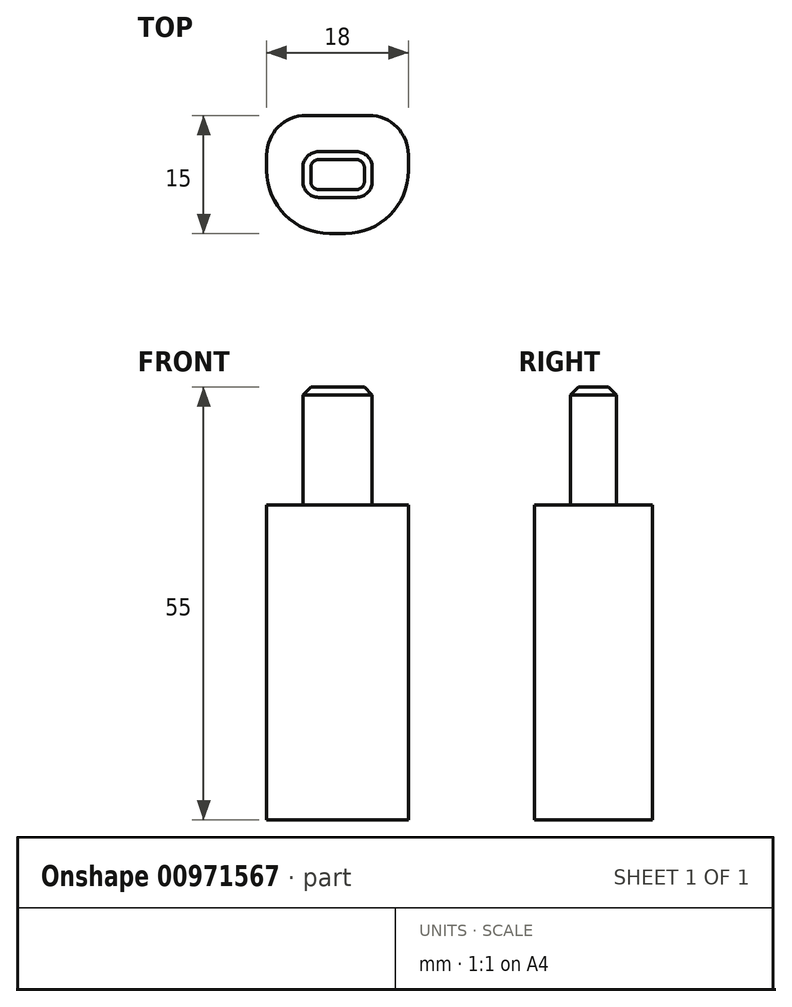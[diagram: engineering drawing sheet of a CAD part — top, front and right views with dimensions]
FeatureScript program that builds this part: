
annotation { "Feature Type Name" : "Feature", "Feature Type Description" : "" }
export const myFeature = defineFeature(function(context is Context, id is Id, definition is map)
    precondition{}
    {
        {
            var Q0;
            Q0=qCreatedBy(makeId("Top.planeOp"),FACE);
            var sketch = newSketch(context, id + "F0", { "sketchPlane" : qUnion([Q0])});
            skLineSegment(sketch, "E0.bottom", {"start": v(-4, 7.5) * mm, "end": v(4, 7.5) * mm});
            skLineSegment(sketch, "E0.top", {"start": v(-1, -7.5) * mm, "end": v(1, -7.5) * mm});
            skLineSegment(sketch, "E0.left", {"start": v(-9, 2.5) * mm, "end": v(-9, 0.5) * mm});
            skLineSegment(sketch, "E0.right", {"start": v(9, 2.5) * mm, "end": v(9, 0.5) * mm});
            skLineSegment(sketch, "E1", {"start": v(-9, -7.5) * mm, "end": v(9, 7.5) * mm, "construction": true});
            skPoint(sketch, "E2.visualSharp", {"position": v(-9, 7.5) * mm});
            skArc(sketch, "E2.filletArc", {"start": v(-4, 7.5) * mm, "mid": v(-7.54, 6.04) * mm, "end": v(-9, 2.5) * mm});
            skPoint(sketch, "E3.visualSharp", {"position": v(9, 7.5) * mm});
            skArc(sketch, "E3.filletArc", {"start": v(9, 2.5) * mm, "mid": v(7.54, 6.04) * mm, "end": v(4, 7.5) * mm});
            skPoint(sketch, "E4.visualSharp", {"position": v(9, -7.5) * mm});
            skArc(sketch, "E4.filletArc", {"start": v(1, -7.5) * mm, "mid": v(6.66, -5.16) * mm, "end": v(9, 0.5) * mm});
            skPoint(sketch, "E5.visualSharp", {"position": v(-9, -7.5) * mm});
            skArc(sketch, "E5.filletArc", {"start": v(-9, 0.5) * mm, "mid": v(-6.66, -5.16) * mm, "end": v(-1, -7.5) * mm});
            skLineSegment(sketch, "E6.bottom", {"start": v(-2.4, 2.9) * mm, "end": v(2.4, 2.9) * mm});
            skLineSegment(sketch, "E6.top", {"start": v(-2.4, -2.9) * mm, "end": v(2.4, -2.9) * mm});
            skLineSegment(sketch, "E6.left", {"start": v(-4.4, 0.9) * mm, "end": v(-4.4, -0.9) * mm});
            skLineSegment(sketch, "E6.right", {"start": v(4.4, 0.9) * mm, "end": v(4.4, -0.9) * mm});
            skLineSegment(sketch, "E7", {"start": v(-4.4, 2.9) * mm, "end": v(4.4, -2.9) * mm, "construction": true});
            skPoint(sketch, "E8.visualSharp", {"position": v(4.4, -2.9) * mm});
            skArc(sketch, "E8.filletArc", {"start": v(2.4, -2.9) * mm, "mid": v(3.81, -2.31) * mm, "end": v(4.4, -0.9) * mm});
            skPoint(sketch, "E9.visualSharp", {"position": v(-4.4, -2.9) * mm});
            skArc(sketch, "E9.filletArc", {"start": v(-4.4, -0.9) * mm, "mid": v(-3.81, -2.31) * mm, "end": v(-2.4, -2.9) * mm});
            skPoint(sketch, "E10.visualSharp", {"position": v(-4.4, 2.9) * mm});
            skArc(sketch, "E10.filletArc", {"start": v(-2.4, 2.9) * mm, "mid": v(-3.81, 2.31) * mm, "end": v(-4.4, 0.9) * mm});
            skPoint(sketch, "E11.visualSharp", {"position": v(4.4, 2.9) * mm});
            skArc(sketch, "E11.filletArc", {"start": v(4.4, 0.9) * mm, "mid": v(3.81, 2.31) * mm, "end": v(2.4, 2.9) * mm});
            skSolve(sketch);
        }
        {
            var Q0;
            Q0=makeQuery(id+"F0.imprint","IMPRINT",FACE,{"disambiguationData":[TD([[makeQuery(id+"F0.imprint","IMPRINT",EDGE,{"derivedFrom":sQuery(id+"F0.wireOp",EDGE,"E0.bottom")}),-1.0]])]});
            var Q1;
            Q1=makeQuery(id+"F0.imprint","IMPRINT",FACE,{"disambiguationData":[TD([[makeQuery(id+"F0.imprint","IMPRINT",EDGE,{"derivedFrom":sQuery(id+"F0.wireOp",EDGE,"E6.bottom")}),-1.0]])]});
            extrude(context, id + "F1", {"entities" : qUnion([Q0, Q1]), "oppositeDirection" : true, "depth" : 40 * mm, "offsetDistance" : 25 * mm});
        }
        {
            var Q0;
            Q0=makeQuery(id+"F0.imprint","IMPRINT",FACE,{"disambiguationData":[TD([[makeQuery(id+"F0.imprint","IMPRINT",EDGE,{"derivedFrom":sQuery(id+"F0.wireOp",EDGE,"E6.bottom")}),-1.0]])]});
            extrude(context, id + "F2", {"entities" : qUnion([Q0]), "operationType" : NewBodyOperationType.ADD, "depth" : 15 * mm, "offsetDistance" : 25 * mm});
        }
        {
            var Q0;
            Q0=makeQuery(id+"F2.opExtrude","CAP_FACE",FACE,{"disambiguationData":[OSD([sQuery(id+"F0.wireOp",EDGE,"E6.bottom"),sQuery(id+"F0.wireOp",EDGE,"E6.top"),sQuery(id+"F0.wireOp",EDGE,"E6.left"),sQuery(id+"F0.wireOp",EDGE,"E6.right"),sQuery(id+"F0.wireOp",EDGE,"E8.filletArc"),sQuery(id+"F0.wireOp",EDGE,"E9.filletArc"),sQuery(id+"F0.wireOp",EDGE,"E10.filletArc"),sQuery(id+"F0.wireOp",EDGE,"E11.filletArc")])],"isStart":false});
            chamfer(context, id + "F3", {"entities" : qUnion([Q0]), "width" : 1 * mm, "tangentPropagation" : true});
        }
    });
